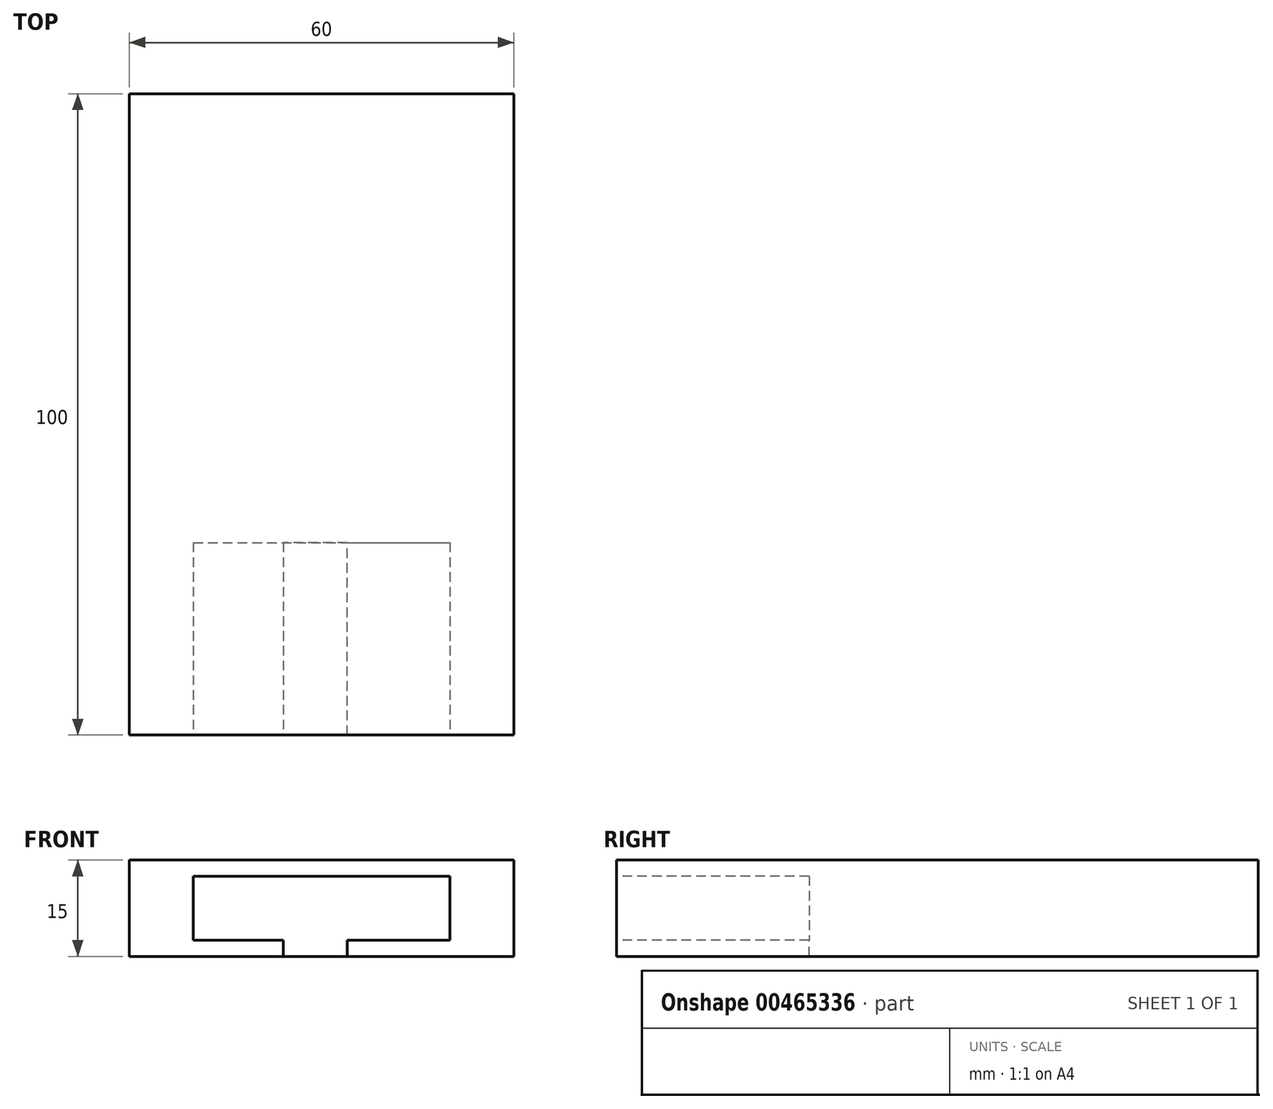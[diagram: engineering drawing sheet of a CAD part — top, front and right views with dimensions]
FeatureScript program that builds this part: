
annotation { "Feature Type Name" : "Feature", "Feature Type Description" : "" }
export const myFeature = defineFeature(function(context is Context, id is Id, definition is map)
    precondition{}
    {
        {
            var Q0;
            Q0=qCreatedBy(makeId("Front.planeOp"),FACE);
            var sketch = newSketch(context, id + "F0", { "sketchPlane" : qUnion([Q0])});
            skLineSegment(sketch, "E0.bottom", {"start": v(-30, 7.5) * mm, "end": v(30, 7.5) * mm});
            skLineSegment(sketch, "E0.top", {"start": v(-30, -7.5) * mm, "end": v(30, -7.5) * mm});
            skLineSegment(sketch, "E0.left", {"start": v(-30, 7.5) * mm, "end": v(-30, -7.5) * mm});
            skLineSegment(sketch, "E0.right", {"start": v(30, 7.5) * mm, "end": v(30, -7.5) * mm});
            skSolve(sketch);
        }
        {
            var Q0;
            Q0=makeQuery(id+"F0.imprint","IMPRINT",FACE,{"disambiguationData":[TD([[makeQuery(id+"F0.imprint","IMPRINT",EDGE,{"derivedFrom":sQuery(id+"F0.wireOp",EDGE,"E0.bottom")}),-1.0]])]});
            extrude(context, id + "F1", {"entities" : qUnion([Q0]), "oppositeDirection" : true, "depth" : 100 * mm});
        }
        {
            var Q0;
            Q0=makeQuery(id+"F1.opExtrude","CAP_FACE",FACE,{"disambiguationData":[OSD([sQuery(id+"F0.wireOp",EDGE,"E0.bottom"),sQuery(id+"F0.wireOp",EDGE,"E0.top"),sQuery(id+"F0.wireOp",EDGE,"E0.left"),sQuery(id+"F0.wireOp",EDGE,"E0.right")])],"isStart":true});
            var sketch = newSketch(context, id + "F2", { "sketchPlane" : qUnion([Q0])});
            skLineSegment(sketch, "E1.bottom", {"start": v(-20, 5) * mm, "end": v(20, 5) * mm});
            skLineSegment(sketch, "E1.top", {"start": v(-20, -5) * mm, "end": v(20, -5) * mm});
            skLineSegment(sketch, "E1.left", {"start": v(-20, 5) * mm, "end": v(-20, -5) * mm});
            skLineSegment(sketch, "E1.right", {"start": v(20, 5) * mm, "end": v(20, -5) * mm});
            skSolve(sketch);
        }
        {
            var Q0;
            Q0=makeQuery(id+"F2.imprint","IMPRINT",FACE,{"disambiguationData":[TD([[makeQuery(id+"F2.imprint","IMPRINT",EDGE,{"derivedFrom":sQuery(id+"F2.wireOp",EDGE,"E1.bottom")}),-1.0]])]});
            extrude(context, id + "F3", {"entities" : qUnion([Q0]), "operationType" : NewBodyOperationType.REMOVE, "oppositeDirection" : true, "depth" : 30 * mm});
        }
        {
            var Q0;
            Q0=makeQuery(id+"F3.boolean.opBoolean","COPY",FACE,{"derivedFrom":makeQuery(id+"F3.opExtrude","SWEPT_FACE",FACE,{"disambiguationData":[OSD([sQuery(id+"F2.wireOp",EDGE,"E1.top")])]})});
            var sketch = newSketch(context, id + "F4", { "sketchPlane" : qUnion([Q0])});
            skLineSegment(sketch, "E2.bottom", {"start": v(-6, 30) * mm, "end": v(4, 30) * mm});
            skLineSegment(sketch, "E2.top", {"start": v(-6, 0) * mm, "end": v(4, 0) * mm});
            skLineSegment(sketch, "E2.left", {"start": v(-6, 30) * mm, "end": v(-6, 0) * mm});
            skLineSegment(sketch, "E2.right", {"start": v(4, 30) * mm, "end": v(4, 0) * mm});
            skSolve(sketch);
        }
        {
            var Q0;
            Q0=makeQuery(id+"F4.imprint","IMPRINT",FACE,{"disambiguationData":[TD([[makeQuery(id+"F4.imprint","IMPRINT",EDGE,{"derivedFrom":sQuery(id+"F4.wireOp",EDGE,"E2.bottom")}),-1.0]])]});
            extrude(context, id + "F5", {"entities" : qUnion([Q0]), "operationType" : NewBodyOperationType.REMOVE, "oppositeDirection" : true, "depth" : 25 * mm});
        }
    });
